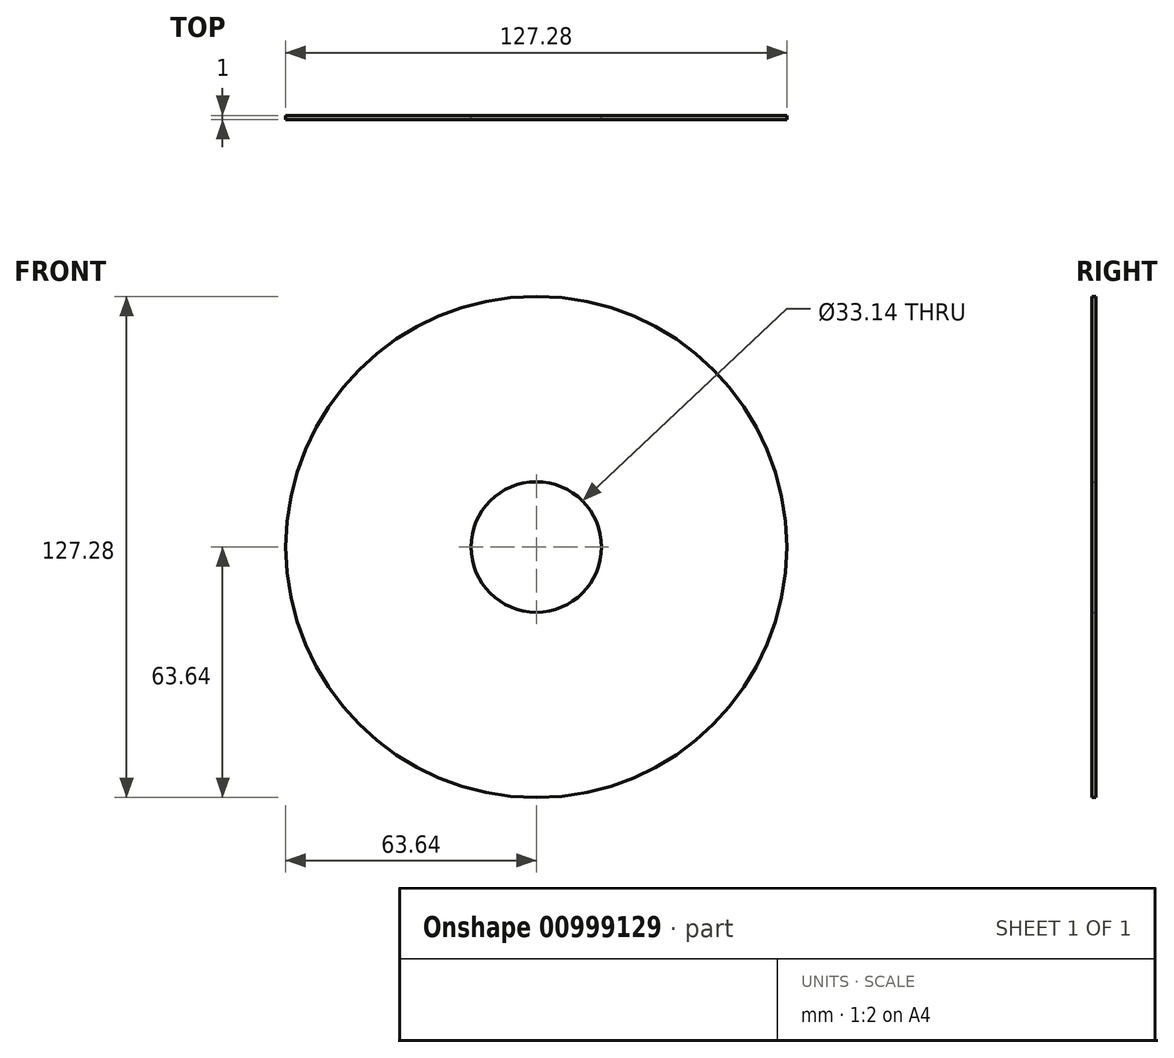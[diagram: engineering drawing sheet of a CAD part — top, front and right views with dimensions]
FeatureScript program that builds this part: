
annotation { "Feature Type Name" : "Feature", "Feature Type Description" : "" }
export const myFeature = defineFeature(function(context is Context, id is Id, definition is map)
    precondition{}
    {
        {
            var Q0;
            Q0=qCreatedBy(makeId("Front.planeOp"),FACE);
            var sketch = newSketch(context, id + "F0", { "sketchPlane" : qUnion([Q0])});
            skCircle(sketch, "E0", {"center": v(0, 0) * mm, "radius": 63.64 * mm});
            skCircle(sketch, "E1", {"center": v(0, 0) * mm, "radius": 16.57 * mm});
            skSolve(sketch);
        }
        {
            var Q0;
            Q0=makeQuery(id+"F0.imprint","IMPRINT",FACE,{"disambiguationData":[TD([[makeQuery(id+"F0.imprint","IMPRINT",EDGE,{"derivedFrom":sQuery(id+"F0.wireOp",EDGE,"E0")}),1.0]])]});
            extrude(context, id + "F1", {"entities" : qUnion([Q0]), "depth" : 1 * mm, "offsetDistance" : 25 * mm});
        }
    });
